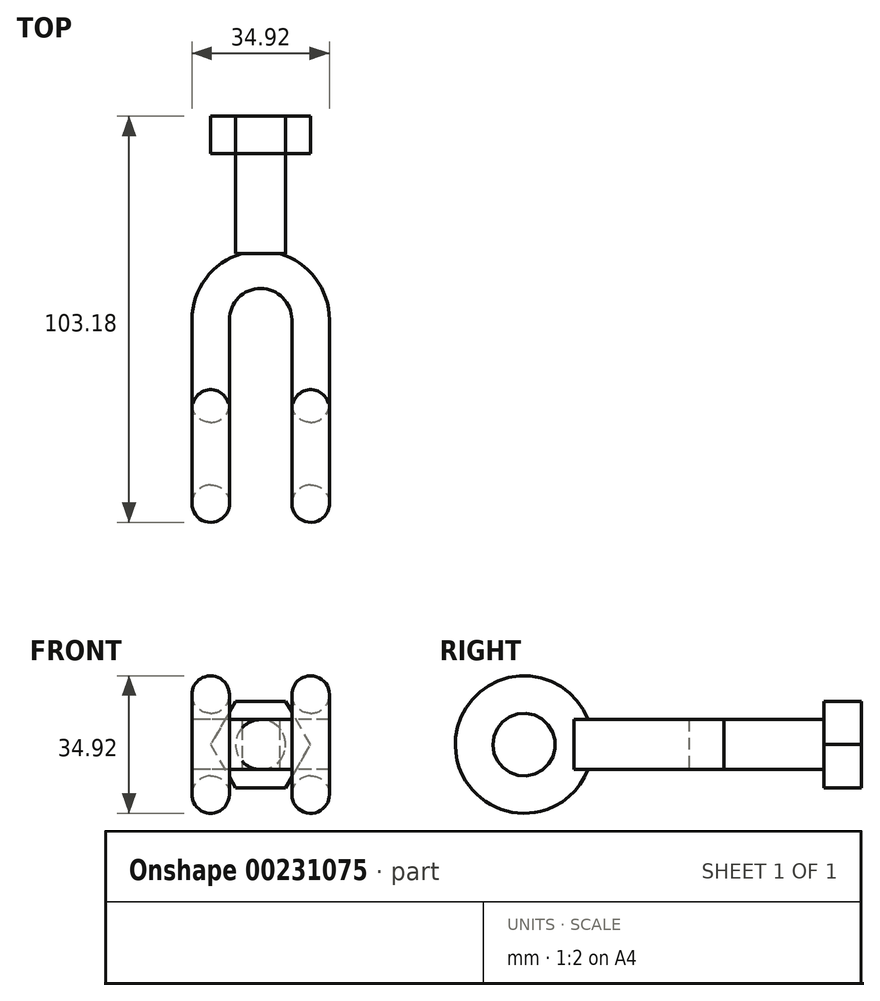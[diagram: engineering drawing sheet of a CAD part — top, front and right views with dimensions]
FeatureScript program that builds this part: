
annotation { "Feature Type Name" : "Feature", "Feature Type Description" : "" }
export const myFeature = defineFeature(function(context is Context, id is Id, definition is map)
    precondition{}
    {
        {
            var Q0;
            Q0=qCreatedBy(makeId("Front.planeOp"),FACE);
            var sketch = newSketch(context, id + "F0", { "sketchPlane" : qUnion([Q0])});
            skLineSegment(sketch, "E0", {"start": v(0, 0) * mm, "end": v(25.4, 0) * mm, "construction": true});
            skCircle(sketch, "E1", {"center": v(0, 12.7) * mm, "radius": 4.76 * mm});
            skCircle(sketch, "E2", {"center": v(25.4, 12.7) * mm, "radius": 4.76 * mm});
            skPoint(sketch, "E3", {"position": v(12.7, 0) * mm});
            skSolve(sketch);
        }
        {
            var Q0;
            Q0 = qSketchRegion(id + "F0", true);
            var Q1;
            Q1=sQuery(id+"F0.wireOp",EDGE,"E0");
            revolve(context, id + "F1", {"entities" : qUnion([Q0]), "axis" : qUnion([Q1]), "revolveType" : RevolveType.FULL});
        }
        {
            var Q0;
            Q0=qCreatedBy(makeId("Top.planeOp"),FACE);
            var sketch = newSketch(context, id + "F2", { "sketchPlane" : qUnion([Q0])});
            skLineSegment(sketch, "E4", {"start": v(-4.76, 12.7) * mm, "end": v(4.76, 12.7) * mm});
            skLineSegment(sketch, "E5", {"start": v(20.64, 12.7) * mm, "end": v(30.16, 12.7) * mm});
            skLineSegment(sketch, "E6", {"start": v(30.16, 12.7) * mm, "end": v(30.16, 34) * mm});
            skLineSegment(sketch, "E7", {"start": v(20.64, 12.7) * mm, "end": v(20.64, 34) * mm});
            skLineSegment(sketch, "E8", {"start": v(4.76, 12.7) * mm, "end": v(4.76, 34) * mm});
            skLineSegment(sketch, "E9", {"start": v(-4.76, 12.7) * mm, "end": v(-4.76, 34) * mm});
            skArc(sketch, "E10", {"start": v(30.16, 34) * mm, "mid": v(26.63, 44.53) * mm, "end": v(17.46, 50.8) * mm});
            skPoint(sketch, "E10.first.point", {"position": v(30.16, 34) * mm});
            skPoint(sketch, "E10.third.point", {"position": v(-4.76, 34) * mm});
            skArc(sketch, "E11", {"start": v(20.64, 34) * mm, "mid": v(12.7, 41.95) * mm, "end": v(4.76, 34) * mm});
            skPoint(sketch, "E11.first.point", {"position": v(20.64, 34) * mm});
            skPoint(sketch, "E11.second.point", {"position": v(13.09, 41.94) * mm});
            skPoint(sketch, "E11.third.point", {"position": v(4.76, 34) * mm});
            skLineSegment(sketch, "E12", {"start": v(17.46, 50.8) * mm, "end": v(7.94, 50.8) * mm});
            skArc(sketch, "E13.trimOffspring", {"start": v(7.94, 50.8) * mm, "mid": v(-1.23, 44.53) * mm, "end": v(-4.76, 34) * mm});
            skSolve(sketch);
        }
        {
            var Q0;
            Q0 = qSketchRegion(id + "F2", true);
            extrude(context, id + "F3", {"entities" : qUnion([Q0]), "operationType" : NewBodyOperationType.ADD, "depth" : 6.35 * mm, "hasSecondDirection" : true, "secondDirectionOppositeDirection" : true, "secondDirectionDepth" : 6.35 * mm});
        }
        {
            var Q0;
            Q0=makeQuery(id+"F3.opExtrude","SWEPT_FACE",FACE,{"disambiguationData":[OSD([sQuery(id+"F2.wireOp",EDGE,"E12")])]});
            var sketch = newSketch(context, id + "F4", { "sketchPlane" : qUnion([Q0])});
            skCircle(sketch, "E14", {"center": v(-12.7, 0) * mm, "radius": 6.35 * mm});
            skSolve(sketch);
        }
        {
            var Q0;
            Q0 = qSketchRegion(id + "F4", true);
            extrude(context, id + "F5", {"entities" : qUnion([Q0]), "operationType" : NewBodyOperationType.ADD, "depth" : 25.4 * mm});
        }
        {
            var Q0;
            Q0=makeQuery(id+"F5.opExtrude","CAP_FACE",FACE,{"disambiguationData":[OSD([sQuery(id+"F4.wireOp",EDGE,"E14")])],"isStart":false});
            var sketch = newSketch(context, id + "F6", { "sketchPlane" : qUnion([Q0])});
            skCircle(sketch, "E15.cCircle", {"center": v(-12.7, 0) * mm, "radius": 11 * mm, "construction": true});
            skLineSegment(sketch, "E15.0", {"start": v(-19.05, 11) * mm, "end": v(-6.35, 11) * mm});
            skLineSegment(sketch, "E15.1", {"start": v(-6.35, 11) * mm, "end": v(0, 0) * mm});
            skLineSegment(sketch, "E15.2", {"start": v(0, 0) * mm, "end": v(-6.35, -11) * mm});
            skLineSegment(sketch, "E15.3", {"start": v(-6.35, -11) * mm, "end": v(-19.05, -11) * mm});
            skLineSegment(sketch, "E15.4", {"start": v(-19.05, -11) * mm, "end": v(-25.4, 0) * mm});
            skLineSegment(sketch, "E15.5", {"start": v(-25.4, 0) * mm, "end": v(-19.05, 11) * mm});
            skPoint(sketch, "E15.0.midPoint", {"position": v(-12.7, 11) * mm});
            skSolve(sketch);
        }
        {
            var Q0;
            Q0 = qSketchRegion(id + "F6", true);
            extrude(context, id + "F7", {"entities" : qUnion([Q0]), "operationType" : NewBodyOperationType.ADD, "depth" : 9.52 * mm});
        }
    });
